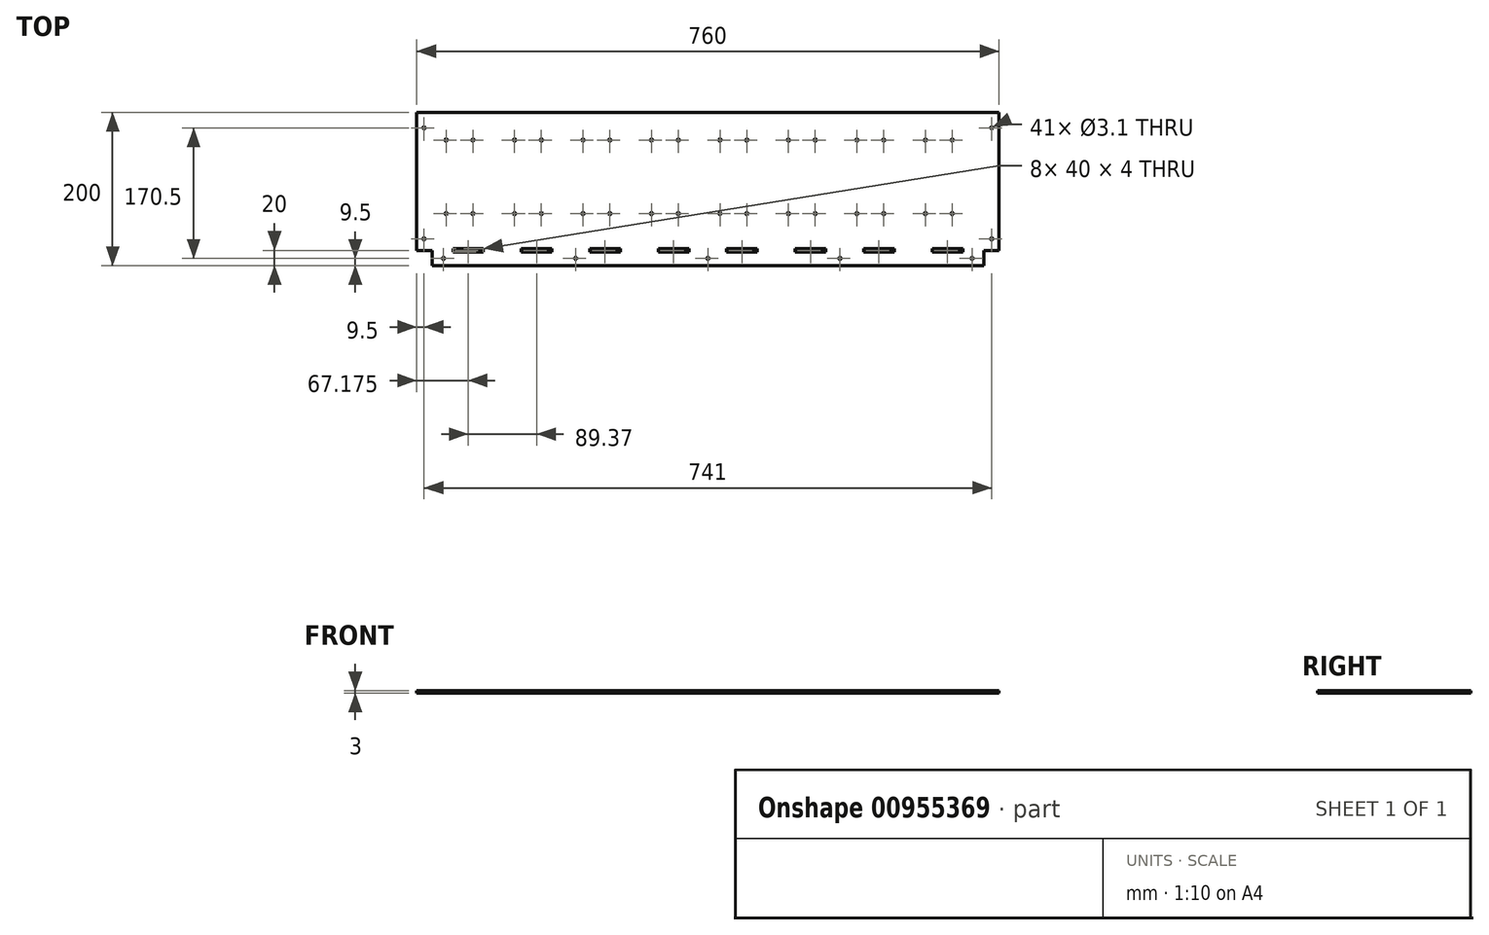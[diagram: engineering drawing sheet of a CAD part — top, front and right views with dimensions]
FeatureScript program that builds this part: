
annotation { "Feature Type Name" : "Feature", "Feature Type Description" : "" }
export const myFeature = defineFeature(function(context is Context, id is Id, definition is map)
    precondition{}
    {
        {
            var Q0;
            Q0=qCreatedBy(makeId("Top.planeOp"),FACE);
            var sketch = newSketch(context, id + "F0", { "sketchPlane" : qUnion([Q0])});
            skLineSegment(sketch, "E0.bottom", {"start": v(-380, -180) * mm, "end": v(380, -180) * mm});
            skLineSegment(sketch, "E0.top", {"start": v(-380, 180) * mm, "end": v(380, 180) * mm});
            skLineSegment(sketch, "E0.left", {"start": v(-380, -180) * mm, "end": v(-380, 180) * mm});
            skLineSegment(sketch, "E0.right", {"start": v(380, -180) * mm, "end": v(380, 180) * mm});
            skPoint(sketch, "E0.middle", {"position": v(0, 0) * mm});
            skSolve(sketch);
        }
        {
            var Q0;
            Q0=makeQuery(id+"F0.imprint","IMPRINT",FACE,{"disambiguationData":[TD([[makeQuery(id+"F0.imprint","IMPRINT",EDGE,{"derivedFrom":sQuery(id+"F0.wireOp",EDGE,"E0.bottom")}),1.0]])]});
            extrude(context, id + "F1", {"entities" : qUnion([Q0]), "endBound" : BoundingType.SYMMETRIC, "depth" : 3 * mm, "offsetDistance" : 25 * mm});
        }
        {
            var Q0;
            Q0=makeQuery(id+"F1.opExtrude","CAP_FACE",FACE,{"disambiguationData":[OSD([sQuery(id+"F0.wireOp",EDGE,"E0.bottom"),sQuery(id+"F0.wireOp",EDGE,"E0.top"),sQuery(id+"F0.wireOp",EDGE,"E0.left"),sQuery(id+"F0.wireOp",EDGE,"E0.right")])],"isStart":false});
            var sketch = newSketch(context, id + "F2", { "sketchPlane" : qUnion([Q0])});
            skLineSegment(sketch, "E1.bottom", {"start": v(-380, -180) * mm, "end": v(-360, -180) * mm});
            skLineSegment(sketch, "E1.top", {"start": v(-380, -160) * mm, "end": v(-360, -160) * mm});
            skLineSegment(sketch, "E1.left", {"start": v(-380, -180) * mm, "end": v(-380, -160) * mm});
            skLineSegment(sketch, "E1.right", {"start": v(-360, -180) * mm, "end": v(-360, -160) * mm});
            skLineSegment(sketch, "E2.bottom", {"start": v(380, -180) * mm, "end": v(360, -180) * mm});
            skLineSegment(sketch, "E2.top", {"start": v(380, -160) * mm, "end": v(360, -160) * mm});
            skLineSegment(sketch, "E2.left", {"start": v(380, -180) * mm, "end": v(380, -160) * mm});
            skLineSegment(sketch, "E2.right", {"start": v(360, -180) * mm, "end": v(360, -160) * mm});
            skLineSegment(sketch, "E3.bottom", {"start": v(380, 180) * mm, "end": v(360, 180) * mm});
            skLineSegment(sketch, "E3.top", {"start": v(380, 160) * mm, "end": v(360, 160) * mm});
            skLineSegment(sketch, "E3.left", {"start": v(380, 180) * mm, "end": v(380, 160) * mm});
            skLineSegment(sketch, "E3.right", {"start": v(360, 180) * mm, "end": v(360, 160) * mm});
            skLineSegment(sketch, "E4.bottom", {"start": v(-380, 180) * mm, "end": v(-360, 180) * mm});
            skLineSegment(sketch, "E4.top", {"start": v(-380, 160) * mm, "end": v(-360, 160) * mm});
            skLineSegment(sketch, "E4.left", {"start": v(-380, 180) * mm, "end": v(-380, 160) * mm});
            skLineSegment(sketch, "E4.right", {"start": v(-360, 180) * mm, "end": v(-360, 160) * mm});
            skSolve(sketch);
        }
        {
            var Q0;
            Q0=makeQuery(id+"F2.imprint","IMPRINT",FACE,{"disambiguationData":[TD([[makeQuery(id+"F2.imprint","IMPRINT",EDGE,{"derivedFrom":sQuery(id+"F2.wireOp",EDGE,"E1.bottom")}),1.0]])]});
            var Q1;
            Q1=makeQuery(id+"F2.imprint","IMPRINT",FACE,{"disambiguationData":[TD([[makeQuery(id+"F2.imprint","IMPRINT",EDGE,{"derivedFrom":sQuery(id+"F2.wireOp",EDGE,"E4.bottom")}),-1.0]])]});
            var Q2;
            Q2=makeQuery(id+"F2.imprint","IMPRINT",FACE,{"disambiguationData":[TD([[makeQuery(id+"F2.imprint","IMPRINT",EDGE,{"derivedFrom":sQuery(id+"F2.wireOp",EDGE,"E2.bottom")}),1.0]])]});
            var Q3;
            Q3=makeQuery(id+"F2.imprint","IMPRINT",FACE,{"disambiguationData":[TD([[makeQuery(id+"F2.imprint","IMPRINT",EDGE,{"derivedFrom":sQuery(id+"F2.wireOp",EDGE,"E3.bottom")}),-1.0]])]});
            extrude(context, id + "F3", {"entities" : qUnion([Q0, Q1, Q2, Q3]), "operationType" : NewBodyOperationType.REMOVE, "endBound" : BoundingType.THROUGH_ALL, "oppositeDirection" : true, "depth" : 25 * mm, "offsetDistance" : 25 * mm});
        }
        {
            var Q0;
            Q0=makeQuery(id+"F1.opExtrude","CAP_FACE",FACE,{"disambiguationData":[OSD([sQuery(id+"F0.wireOp",EDGE,"E0.bottom"),sQuery(id+"F0.wireOp",EDGE,"E0.top"),sQuery(id+"F0.wireOp",EDGE,"E0.left"),sQuery(id+"F0.wireOp",EDGE,"E0.right")])],"isStart":false});
            var sketch = newSketch(context, id + "F4", { "sketchPlane" : qUnion([Q0])});
            skCircle(sketch, "E5", {"center": v(-370.5, 145) * mm, "radius": 1.55 * mm});
            skCircle(sketch, "E6", {"center": v(-370.5, 0) * mm, "radius": 1.55 * mm});
            skCircle(sketch, "E7", {"center": v(-370.5, -145) * mm, "radius": 1.55 * mm});
            skCircle(sketch, "E8", {"center": v(370.5, -145) * mm, "radius": 1.55 * mm});
            skCircle(sketch, "E9", {"center": v(370.5, 0) * mm, "radius": 1.55 * mm});
            skCircle(sketch, "E10", {"center": v(370.5, 145) * mm, "radius": 1.55 * mm});
            skCircle(sketch, "E11", {"center": v(0, 170.5) * mm, "radius": 1.55 * mm});
            skCircle(sketch, "E12", {"center": v(172.5, 170.5) * mm, "radius": 1.55 * mm});
            skCircle(sketch, "E13", {"center": v(345, 170.5) * mm, "radius": 1.55 * mm});
            skCircle(sketch, "E14", {"center": v(-172.5, 170.5) * mm, "radius": 1.55 * mm});
            skCircle(sketch, "E15", {"center": v(-345, 170.5) * mm, "radius": 1.55 * mm});
            skCircle(sketch, "E16", {"center": v(-345, -170.5) * mm, "radius": 1.55 * mm});
            skCircle(sketch, "E17", {"center": v(-172.5, -170.5) * mm, "radius": 1.55 * mm});
            skCircle(sketch, "E18", {"center": v(0, -170.5) * mm, "radius": 1.55 * mm});
            skCircle(sketch, "E19", {"center": v(172.5, -170.5) * mm, "radius": 1.55 * mm});
            skCircle(sketch, "E20", {"center": v(345, -170.5) * mm, "radius": 1.55 * mm});
            skLineSegment(sketch, "E21", {"start": v(-345, 170.5) * mm, "end": v(-172.5, 170.5) * mm, "construction": true});
            skLineSegment(sketch, "E22", {"start": v(-172.5, 170.5) * mm, "end": v(0, 170.5) * mm, "construction": true});
            skLineSegment(sketch, "E23", {"start": v(0, 170.5) * mm, "end": v(172.5, 170.5) * mm, "construction": true});
            skLineSegment(sketch, "E24", {"start": v(172.5, 170.5) * mm, "end": v(345, 170.5) * mm, "construction": true});
            skSolve(sketch);
        }
        {
            var Q0;
            Q0=qSketchRegion(id+"F4",true);
            extrude(context, id + "F5", {"entities" : qUnion([Q0]), "operationType" : NewBodyOperationType.REMOVE, "endBound" : BoundingType.THROUGH_ALL, "oppositeDirection" : true, "depth" : 25 * mm, "offsetDistance" : 25 * mm});
        }
        {
            var Q0;
            Q0=makeQuery(id+"F1.opExtrude","CAP_FACE",FACE,{"disambiguationData":[OSD([sQuery(id+"F0.wireOp",EDGE,"E0.bottom"),sQuery(id+"F0.wireOp",EDGE,"E0.top"),sQuery(id+"F0.wireOp",EDGE,"E0.left"),sQuery(id+"F0.wireOp",EDGE,"E0.right")])],"isStart":false});
            var sketch = newSketch(context, id + "F6", { "sketchPlane" : qUnion([Q0])});
            skLineSegment(sketch, "E25.bottom", {"start": v(-259.76, 120) * mm, "end": v(-209.76, 120) * mm});
            skLineSegment(sketch, "E25.top", {"start": v(-259.76, 100) * mm, "end": v(-209.76, 100) * mm});
            skLineSegment(sketch, "E25.left", {"start": v(-259.76, 120) * mm, "end": v(-259.76, 100) * mm});
            skLineSegment(sketch, "E25.right", {"start": v(-209.76, 120) * mm, "end": v(-209.76, 100) * mm});
            skLineSegment(sketch, "E26.bottom", {"start": v(-168.66, 120) * mm, "end": v(-118.66, 120) * mm});
            skLineSegment(sketch, "E26.top", {"start": v(-168.66, 100) * mm, "end": v(-118.66, 100) * mm});
            skLineSegment(sketch, "E26.left", {"start": v(-168.66, 120) * mm, "end": v(-168.66, 100) * mm});
            skLineSegment(sketch, "E26.right", {"start": v(-118.66, 120) * mm, "end": v(-118.66, 100) * mm});
            skLineSegment(sketch, "E27.bottom", {"start": v(-77.55, 120) * mm, "end": v(-27.55, 120) * mm});
            skLineSegment(sketch, "E27.top", {"start": v(-77.55, 100) * mm, "end": v(-27.55, 100) * mm});
            skLineSegment(sketch, "E27.left", {"start": v(-77.55, 120) * mm, "end": v(-77.55, 100) * mm});
            skLineSegment(sketch, "E27.right", {"start": v(-27.55, 120) * mm, "end": v(-27.55, 100) * mm});
            skLineSegment(sketch, "E28.bottom", {"start": v(100, 120) * mm, "end": v(150, 120) * mm});
            skLineSegment(sketch, "E28.top", {"start": v(100, 100) * mm, "end": v(150, 100) * mm});
            skLineSegment(sketch, "E28.left", {"start": v(100, 120) * mm, "end": v(100, 100) * mm});
            skLineSegment(sketch, "E28.right", {"start": v(150, 120) * mm, "end": v(150, 100) * mm});
            skLineSegment(sketch, "E29.bottom", {"start": v(200, 120) * mm, "end": v(250, 120) * mm});
            skLineSegment(sketch, "E29.top", {"start": v(200, 100) * mm, "end": v(250, 100) * mm});
            skLineSegment(sketch, "E29.left", {"start": v(200, 120) * mm, "end": v(200, 100) * mm});
            skLineSegment(sketch, "E29.right", {"start": v(250, 120) * mm, "end": v(250, 100) * mm});
            skLineSegment(sketch, "E30.bottom", {"start": v(300, 120) * mm, "end": v(350, 120) * mm});
            skLineSegment(sketch, "E30.top", {"start": v(300, 100) * mm, "end": v(350, 100) * mm});
            skLineSegment(sketch, "E30.left", {"start": v(300, 120) * mm, "end": v(300, 100) * mm});
            skLineSegment(sketch, "E30.right", {"start": v(350, 120) * mm, "end": v(350, 100) * mm});
            skLineSegment(sketch, "E31.bottom", {"start": v(-5, 120) * mm, "end": v(45, 120) * mm});
            skLineSegment(sketch, "E31.top", {"start": v(-5, 100) * mm, "end": v(45, 100) * mm});
            skLineSegment(sketch, "E31.left", {"start": v(-5, 120) * mm, "end": v(-5, 100) * mm});
            skLineSegment(sketch, "E31.right", {"start": v(45, 120) * mm, "end": v(45, 100) * mm});
            skLineSegment(sketch, "E32.bottom", {"start": v(-350.87, 120) * mm, "end": v(-300.87, 120) * mm});
            skLineSegment(sketch, "E32.top", {"start": v(-350.87, 100) * mm, "end": v(-300.87, 100) * mm});
            skLineSegment(sketch, "E32.left", {"start": v(-350.87, 120) * mm, "end": v(-350.87, 100) * mm});
            skLineSegment(sketch, "E32.right", {"start": v(-300.87, 120) * mm, "end": v(-300.87, 100) * mm});
            skSolve(sketch);
        }
        {
            var Q0;
            Q0 = qSketchRegion(id + "F6", true);
            extrude(context, id + "F7", {"entities" : qUnion([Q0]), "operationType" : NewBodyOperationType.REMOVE, "endBound" : BoundingType.THROUGH_ALL, "oppositeDirection" : true, "depth" : 25 * mm, "offsetDistance" : 25 * mm});
        }
        {
            var Q0;
            Q0=makeQuery(id+"F1.opExtrude","CAP_FACE",FACE,{"disambiguationData":[OSD([sQuery(id+"F0.wireOp",EDGE,"E0.bottom"),sQuery(id+"F0.wireOp",EDGE,"E0.top"),sQuery(id+"F0.wireOp",EDGE,"E0.left"),sQuery(id+"F0.wireOp",EDGE,"E0.right")])],"isStart":false});
            var sketch = newSketch(context, id + "F8", { "sketchPlane" : qUnion([Q0])});
            skLineSegment(sketch, "E33.bottom", {"start": v(-345.88, 14) * mm, "end": v(-302.38, 14) * mm, "construction": true});
            skLineSegment(sketch, "E33.top", {"start": v(-345.88, -116) * mm, "end": v(-302.38, -116) * mm, "construction": true});
            skLineSegment(sketch, "E33.left", {"start": v(-345.88, 14) * mm, "end": v(-345.88, -116) * mm, "construction": true});
            skLineSegment(sketch, "E33.right", {"start": v(-302.38, 14) * mm, "end": v(-302.38, -116) * mm, "construction": true});
            skLineSegment(sketch, "E34.bottom", {"start": v(-256.51, 14) * mm, "end": v(-213.01, 14) * mm, "construction": true});
            skLineSegment(sketch, "E34.top", {"start": v(-256.51, -116) * mm, "end": v(-213.01, -116) * mm, "construction": true});
            skLineSegment(sketch, "E34.left", {"start": v(-256.51, 14) * mm, "end": v(-256.51, -116) * mm, "construction": true});
            skLineSegment(sketch, "E34.right", {"start": v(-213.01, 14) * mm, "end": v(-213.01, -116) * mm, "construction": true});
            skLineSegment(sketch, "E35.bottom", {"start": v(-167.14, 14) * mm, "end": v(-123.64, 14) * mm, "construction": true});
            skLineSegment(sketch, "E35.top", {"start": v(-167.14, -116) * mm, "end": v(-123.64, -116) * mm, "construction": true});
            skLineSegment(sketch, "E35.left", {"start": v(-167.14, 14) * mm, "end": v(-167.14, -116) * mm, "construction": true});
            skLineSegment(sketch, "E35.right", {"start": v(-123.64, 14) * mm, "end": v(-123.64, -116) * mm, "construction": true});
            skLineSegment(sketch, "E36.bottom", {"start": v(-77.77, 14) * mm, "end": v(-34.27, 14) * mm, "construction": true});
            skLineSegment(sketch, "E36.top", {"start": v(-77.77, -116) * mm, "end": v(-34.27, -116) * mm, "construction": true});
            skLineSegment(sketch, "E36.left", {"start": v(-77.77, 14) * mm, "end": v(-77.77, -116) * mm, "construction": true});
            skLineSegment(sketch, "E36.right", {"start": v(-34.27, 14) * mm, "end": v(-34.27, -116) * mm, "construction": true});
            skLineSegment(sketch, "E37.bottom", {"start": v(11.6, 14) * mm, "end": v(55.1, 14) * mm, "construction": true});
            skLineSegment(sketch, "E37.top", {"start": v(11.6, -116) * mm, "end": v(55.1, -116) * mm, "construction": true});
            skLineSegment(sketch, "E37.left", {"start": v(11.6, 14) * mm, "end": v(11.6, -116) * mm, "construction": true});
            skLineSegment(sketch, "E37.right", {"start": v(55.1, 14) * mm, "end": v(55.1, -116) * mm, "construction": true});
            skLineSegment(sketch, "E38.bottom", {"start": v(100.97, 14) * mm, "end": v(144.47, 14) * mm, "construction": true});
            skLineSegment(sketch, "E38.top", {"start": v(100.97, -116) * mm, "end": v(144.47, -116) * mm, "construction": true});
            skLineSegment(sketch, "E38.left", {"start": v(100.97, 14) * mm, "end": v(100.97, -116) * mm, "construction": true});
            skLineSegment(sketch, "E38.right", {"start": v(144.47, 14) * mm, "end": v(144.47, -116) * mm, "construction": true});
            skLineSegment(sketch, "E39.bottom", {"start": v(190.34, 14) * mm, "end": v(233.84, 14) * mm, "construction": true});
            skLineSegment(sketch, "E39.top", {"start": v(190.34, -116) * mm, "end": v(233.84, -116) * mm, "construction": true});
            skLineSegment(sketch, "E39.left", {"start": v(190.34, 14) * mm, "end": v(190.34, -116) * mm, "construction": true});
            skLineSegment(sketch, "E39.right", {"start": v(233.84, 14) * mm, "end": v(233.84, -116) * mm, "construction": true});
            skLineSegment(sketch, "E40.bottom", {"start": v(279.7, 14) * mm, "end": v(323.2, 14) * mm, "construction": true});
            skLineSegment(sketch, "E40.top", {"start": v(279.7, -116) * mm, "end": v(323.2, -116) * mm, "construction": true});
            skLineSegment(sketch, "E40.left", {"start": v(279.7, 14) * mm, "end": v(279.7, -116) * mm, "construction": true});
            skLineSegment(sketch, "E40.right", {"start": v(323.2, 14) * mm, "end": v(323.2, -116) * mm, "construction": true});
            skCircle(sketch, "E41", {"center": v(-341.63, -16) * mm, "radius": 1.55 * mm});
            skCircle(sketch, "E42", {"center": v(-306.63, -16) * mm, "radius": 1.55 * mm});
            skCircle(sketch, "E43", {"center": v(-341.63, -112) * mm, "radius": 1.55 * mm});
            skCircle(sketch, "E44", {"center": v(-306.63, -112) * mm, "radius": 1.55 * mm});
            skCircle(sketch, "E45", {"center": v(-252.26, -112) * mm, "radius": 1.55 * mm});
            skCircle(sketch, "E46", {"center": v(-217.26, -112) * mm, "radius": 1.55 * mm});
            skCircle(sketch, "E47", {"center": v(-252.26, -16) * mm, "radius": 1.55 * mm});
            skCircle(sketch, "E48", {"center": v(-217.26, -16) * mm, "radius": 1.55 * mm});
            skCircle(sketch, "E49", {"center": v(-162.9, -16) * mm, "radius": 1.55 * mm});
            skCircle(sketch, "E50", {"center": v(-127.9, -16) * mm, "radius": 1.55 * mm});
            skCircle(sketch, "E51", {"center": v(-162.9, -112) * mm, "radius": 1.55 * mm});
            skCircle(sketch, "E52", {"center": v(-127.9, -112) * mm, "radius": 1.55 * mm});
            skCircle(sketch, "E53", {"center": v(-73.52, -112) * mm, "radius": 1.55 * mm});
            skCircle(sketch, "E54", {"center": v(-38.52, -112) * mm, "radius": 1.55 * mm});
            skCircle(sketch, "E55", {"center": v(-73.52, -16) * mm, "radius": 1.55 * mm});
            skCircle(sketch, "E56", {"center": v(-38.52, -16) * mm, "radius": 1.55 * mm});
            skCircle(sketch, "E57", {"center": v(15.85, -16) * mm, "radius": 1.55 * mm});
            skCircle(sketch, "E58", {"center": v(50.85, -16) * mm, "radius": 1.55 * mm});
            skCircle(sketch, "E59", {"center": v(15.85, -112) * mm, "radius": 1.55 * mm});
            skCircle(sketch, "E60", {"center": v(50.85, -112) * mm, "radius": 1.55 * mm});
            skCircle(sketch, "E61", {"center": v(105.22, -112) * mm, "radius": 1.55 * mm});
            skCircle(sketch, "E62", {"center": v(140.22, -112) * mm, "radius": 1.55 * mm});
            skCircle(sketch, "E63", {"center": v(105.22, -16) * mm, "radius": 1.55 * mm});
            skCircle(sketch, "E64", {"center": v(140.22, -16) * mm, "radius": 1.55 * mm});
            skCircle(sketch, "E65", {"center": v(194.59, -16) * mm, "radius": 1.55 * mm});
            skCircle(sketch, "E66", {"center": v(229.59, -16) * mm, "radius": 1.55 * mm});
            skCircle(sketch, "E67", {"center": v(194.59, -112) * mm, "radius": 1.55 * mm});
            skCircle(sketch, "E68", {"center": v(229.59, -112) * mm, "radius": 1.55 * mm});
            skCircle(sketch, "E69", {"center": v(283.96, -112) * mm, "radius": 1.55 * mm});
            skCircle(sketch, "E70", {"center": v(318.96, -112) * mm, "radius": 1.55 * mm});
            skCircle(sketch, "E71", {"center": v(283.96, -16) * mm, "radius": 1.55 * mm});
            skCircle(sketch, "E72", {"center": v(318.96, -16) * mm, "radius": 1.55 * mm});
            skLineSegment(sketch, "E73.bottom", {"start": v(-333.53, -9.38) * mm, "end": v(-326.08, -9.38) * mm, "construction": true});
            skLineSegment(sketch, "E73.top", {"start": v(-333.53, -115) * mm, "end": v(-326.08, -115) * mm, "construction": true});
            skLineSegment(sketch, "E73.left", {"start": v(-333.53, -9.38) * mm, "end": v(-333.53, -115) * mm, "construction": true});
            skLineSegment(sketch, "E73.right", {"start": v(-326.08, -9.38) * mm, "end": v(-326.08, -115) * mm, "construction": true});
            skLineSegment(sketch, "E74.bottom", {"start": v(-244.16, 7.66) * mm, "end": v(-236.71, 7.66) * mm, "construction": true});
            skLineSegment(sketch, "E74.top", {"start": v(-244.16, -97.96) * mm, "end": v(-236.71, -97.96) * mm, "construction": true});
            skLineSegment(sketch, "E74.left", {"start": v(-244.16, 7.66) * mm, "end": v(-244.16, -97.96) * mm, "construction": true});
            skLineSegment(sketch, "E74.right", {"start": v(-236.71, 7.66) * mm, "end": v(-236.71, -97.96) * mm, "construction": true});
            skLineSegment(sketch, "E75.bottom", {"start": v(-154.8, 2.48) * mm, "end": v(-147.34, 2.48) * mm, "construction": true});
            skLineSegment(sketch, "E75.top", {"start": v(-154.8, -103.14) * mm, "end": v(-147.34, -103.14) * mm, "construction": true});
            skLineSegment(sketch, "E75.left", {"start": v(-154.8, 2.48) * mm, "end": v(-154.8, -103.14) * mm, "construction": true});
            skLineSegment(sketch, "E75.right", {"start": v(-147.34, 2.48) * mm, "end": v(-147.34, -103.14) * mm, "construction": true});
            skLineSegment(sketch, "E76.bottom", {"start": v(-65.42, 2.85) * mm, "end": v(-57.97, 2.85) * mm, "construction": true});
            skLineSegment(sketch, "E76.top", {"start": v(-65.42, -102.77) * mm, "end": v(-57.97, -102.77) * mm, "construction": true});
            skLineSegment(sketch, "E76.left", {"start": v(-65.42, 2.85) * mm, "end": v(-65.42, -102.77) * mm, "construction": true});
            skLineSegment(sketch, "E76.right", {"start": v(-57.97, 2.85) * mm, "end": v(-57.97, -102.77) * mm, "construction": true});
            skLineSegment(sketch, "E77.bottom", {"start": v(23.95, 0.03) * mm, "end": v(31.4, 0.03) * mm, "construction": true});
            skLineSegment(sketch, "E77.top", {"start": v(23.95, -105.6) * mm, "end": v(31.4, -105.6) * mm, "construction": true});
            skLineSegment(sketch, "E77.left", {"start": v(23.95, 0.03) * mm, "end": v(23.95, -105.6) * mm, "construction": true});
            skLineSegment(sketch, "E77.right", {"start": v(31.4, 0.03) * mm, "end": v(31.4, -105.6) * mm, "construction": true});
            skLineSegment(sketch, "E78.bottom", {"start": v(113.32, -0.35) * mm, "end": v(120.77, -0.35) * mm, "construction": true});
            skLineSegment(sketch, "E78.top", {"start": v(113.32, -105.97) * mm, "end": v(120.77, -105.97) * mm, "construction": true});
            skLineSegment(sketch, "E78.left", {"start": v(113.32, -0.35) * mm, "end": v(113.32, -105.97) * mm, "construction": true});
            skLineSegment(sketch, "E78.right", {"start": v(120.77, -0.35) * mm, "end": v(120.77, -105.97) * mm, "construction": true});
            skLineSegment(sketch, "E79.bottom", {"start": v(202.69, 3.6) * mm, "end": v(210.14, 3.6) * mm, "construction": true});
            skLineSegment(sketch, "E79.top", {"start": v(202.69, -102.02) * mm, "end": v(210.14, -102.02) * mm, "construction": true});
            skLineSegment(sketch, "E79.left", {"start": v(202.69, 3.6) * mm, "end": v(202.69, -102.02) * mm, "construction": true});
            skLineSegment(sketch, "E79.right", {"start": v(210.14, 3.6) * mm, "end": v(210.14, -102.02) * mm, "construction": true});
            skLineSegment(sketch, "E80.bottom", {"start": v(292.06, 2.29) * mm, "end": v(299.5, 2.29) * mm, "construction": true});
            skLineSegment(sketch, "E80.top", {"start": v(292.06, -103.33) * mm, "end": v(299.5, -103.33) * mm, "construction": true});
            skLineSegment(sketch, "E80.left", {"start": v(292.06, 2.29) * mm, "end": v(292.06, -103.33) * mm, "construction": true});
            skLineSegment(sketch, "E80.right", {"start": v(299.5, 2.29) * mm, "end": v(299.5, -103.33) * mm, "construction": true});
            skLineSegment(sketch, "E81", {"start": v(-360, -161) * mm, "end": v(-243.49, -161) * mm, "construction": true});
            skLineSegment(sketch, "E82.bottom", {"start": v(-330.6, 0) * mm, "end": v(-328.99, 0) * mm, "construction": true});
            skLineSegment(sketch, "E82.top", {"start": v(-330.6, -84.3) * mm, "end": v(-328.99, -84.3) * mm, "construction": true});
            skLineSegment(sketch, "E82.left", {"start": v(-330.6, 0) * mm, "end": v(-330.6, -84.3) * mm, "construction": true});
            skLineSegment(sketch, "E82.right", {"start": v(-328.99, 0) * mm, "end": v(-328.99, -84.3) * mm, "construction": true});
            skSolve(sketch);
        }
        {
            var Q0;
            Q0 = qSketchRegion(id + "F8", true);
            extrude(context, id + "F9", {"entities" : qUnion([Q0]), "operationType" : NewBodyOperationType.REMOVE, "endBound" : BoundingType.THROUGH_ALL, "oppositeDirection" : true, "depth" : 25 * mm, "offsetDistance" : 25 * mm});
        }
        {
            var Q0;
            Q0=makeQuery(id+"F1.opExtrude","CAP_FACE",FACE,{"disambiguationData":[OSD([sQuery(id+"F0.wireOp",EDGE,"E0.bottom"),sQuery(id+"F0.wireOp",EDGE,"E0.top"),sQuery(id+"F0.wireOp",EDGE,"E0.left"),sQuery(id+"F0.wireOp",EDGE,"E0.right")])],"isStart":false});
            var sketch = newSketch(context, id + "F10", { "sketchPlane" : qUnion([Q0])});
            skLineSegment(sketch, "E83.bottom", {"start": v(-332.83, -158) * mm, "end": v(-292.83, -158) * mm});
            skLineSegment(sketch, "E83.top", {"start": v(-332.83, -162) * mm, "end": v(-292.83, -162) * mm});
            skLineSegment(sketch, "E83.left", {"start": v(-332.83, -158) * mm, "end": v(-332.83, -162) * mm});
            skLineSegment(sketch, "E83.right", {"start": v(-292.83, -158) * mm, "end": v(-292.83, -162) * mm});
            skLineSegment(sketch, "E84.bottom", {"start": v(-243.46, -158) * mm, "end": v(-203.46, -158) * mm});
            skLineSegment(sketch, "E84.top", {"start": v(-243.46, -162) * mm, "end": v(-203.46, -162) * mm});
            skLineSegment(sketch, "E84.left", {"start": v(-243.46, -158) * mm, "end": v(-243.46, -162) * mm});
            skLineSegment(sketch, "E84.right", {"start": v(-203.46, -158) * mm, "end": v(-203.46, -162) * mm});
            skLineSegment(sketch, "E85.bottom", {"start": v(-154.09, -158) * mm, "end": v(-114.09, -158) * mm});
            skLineSegment(sketch, "E85.top", {"start": v(-154.09, -162) * mm, "end": v(-114.09, -162) * mm});
            skLineSegment(sketch, "E85.left", {"start": v(-154.09, -158) * mm, "end": v(-154.09, -162) * mm});
            skLineSegment(sketch, "E85.right", {"start": v(-114.09, -158) * mm, "end": v(-114.09, -162) * mm});
            skLineSegment(sketch, "E86.bottom", {"start": v(-64.72, -158) * mm, "end": v(-24.72, -158) * mm});
            skLineSegment(sketch, "E86.top", {"start": v(-64.72, -162) * mm, "end": v(-24.72, -162) * mm});
            skLineSegment(sketch, "E86.left", {"start": v(-64.72, -158) * mm, "end": v(-64.72, -162) * mm});
            skLineSegment(sketch, "E86.right", {"start": v(-24.72, -158) * mm, "end": v(-24.72, -162) * mm});
            skLineSegment(sketch, "E87.bottom", {"start": v(24.65, -158) * mm, "end": v(64.65, -158) * mm});
            skLineSegment(sketch, "E87.top", {"start": v(24.65, -162) * mm, "end": v(64.65, -162) * mm});
            skLineSegment(sketch, "E87.left", {"start": v(24.65, -158) * mm, "end": v(24.65, -162) * mm});
            skLineSegment(sketch, "E87.right", {"start": v(64.65, -158) * mm, "end": v(64.65, -162) * mm});
            skLineSegment(sketch, "E88.bottom", {"start": v(114.02, -158) * mm, "end": v(154.02, -158) * mm});
            skLineSegment(sketch, "E88.top", {"start": v(114.02, -162) * mm, "end": v(154.02, -162) * mm});
            skLineSegment(sketch, "E88.left", {"start": v(114.02, -158) * mm, "end": v(114.02, -162) * mm});
            skLineSegment(sketch, "E88.right", {"start": v(154.02, -158) * mm, "end": v(154.02, -162) * mm});
            skLineSegment(sketch, "E89.bottom", {"start": v(203.4, -158) * mm, "end": v(243.4, -158) * mm});
            skLineSegment(sketch, "E89.top", {"start": v(203.4, -162) * mm, "end": v(243.4, -162) * mm});
            skLineSegment(sketch, "E89.left", {"start": v(203.4, -158) * mm, "end": v(203.4, -162) * mm});
            skLineSegment(sketch, "E89.right", {"start": v(243.4, -158) * mm, "end": v(243.4, -162) * mm});
            skLineSegment(sketch, "E90.bottom", {"start": v(292.76, -158) * mm, "end": v(332.76, -158) * mm});
            skLineSegment(sketch, "E90.top", {"start": v(292.76, -162) * mm, "end": v(332.76, -162) * mm});
            skLineSegment(sketch, "E90.left", {"start": v(292.76, -158) * mm, "end": v(292.76, -162) * mm});
            skLineSegment(sketch, "E90.right", {"start": v(332.76, -158) * mm, "end": v(332.76, -162) * mm});
            skLineSegment(sketch, "E91", {"start": v(-360, -161) * mm, "end": v(-137.49, -161) * mm, "construction": true});
            skSolve(sketch);
        }
        {
            var Q0;
            Q0 = qSketchRegion(id + "F10", true);
            extrude(context, id + "F11", {"entities" : qUnion([Q0]), "operationType" : NewBodyOperationType.REMOVE, "endBound" : BoundingType.THROUGH_ALL, "oppositeDirection" : true, "depth" : 25 * mm, "offsetDistance" : 25 * mm});
        }
        {
            var Q0;
            Q0=makeQuery(id+"F1.opExtrude","CAP_FACE",FACE,{"disambiguationData":[OSD([sQuery(id+"F0.wireOp",EDGE,"E0.bottom"),sQuery(id+"F0.wireOp",EDGE,"E0.top"),sQuery(id+"F0.wireOp",EDGE,"E0.left"),sQuery(id+"F0.wireOp",EDGE,"E0.right")])],"isStart":false});
            var sketch = newSketch(context, id + "F12", { "sketchPlane" : qUnion([Q0])});
            skLineSegment(sketch, "E92.bottom", {"start": v(-380, 20) * mm, "end": v(380, 20) * mm});
            skLineSegment(sketch, "E92.top", {"start": v(-380, 180) * mm, "end": v(380, 180) * mm});
            skLineSegment(sketch, "E92.left", {"start": v(-380, 20) * mm, "end": v(-380, 180) * mm});
            skLineSegment(sketch, "E92.right", {"start": v(380, 20) * mm, "end": v(380, 180) * mm});
            skSolve(sketch);
        }
        {
            var Q0;
            Q0 = qSketchRegion(id + "F12", true);
            extrude(context, id + "F13", {"entities" : qUnion([Q0]), "operationType" : NewBodyOperationType.REMOVE, "endBound" : BoundingType.THROUGH_ALL, "oppositeDirection" : true, "depth" : 25 * mm, "offsetDistance" : 25 * mm});
        }
    });
